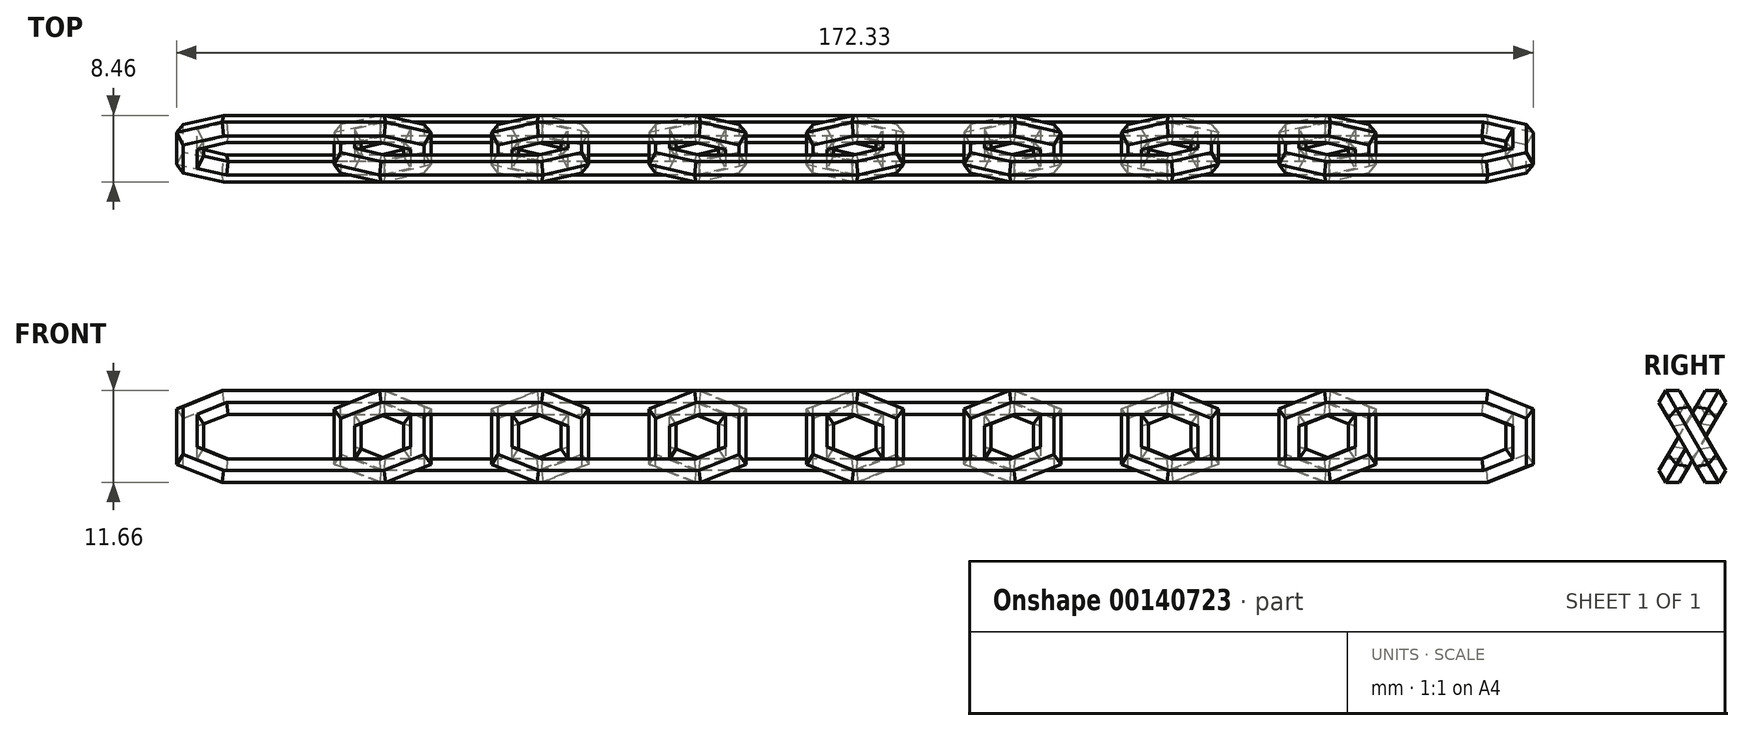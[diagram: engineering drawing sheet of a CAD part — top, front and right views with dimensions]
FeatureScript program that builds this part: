
annotation { "Feature Type Name" : "Feature", "Feature Type Description" : "" }
export const myFeature = defineFeature(function(context is Context, id is Id, definition is map)
    precondition{}
    {
        {
            var Q0;
            Q0=qCreatedBy(makeId("Front.planeOp"),FACE);
            var sketch = newSketch(context, id + "F0", { "sketchPlane" : qUnion([Q0])});
            skCircle(sketch, "E0.cCircle", {"center": v(-58.85, 0) * mm, "radius": 1.5 * mm, "construction": true});
            skLineSegment(sketch, "E0.0", {"start": v(-57.98, 1.5) * mm, "end": v(-57.12, 0) * mm});
            skLineSegment(sketch, "E0.1", {"start": v(-57.12, 0) * mm, "end": v(-57.98, -1.5) * mm});
            skLineSegment(sketch, "E0.2", {"start": v(-57.98, -1.5) * mm, "end": v(-59.72, -1.5) * mm});
            skLineSegment(sketch, "E0.3", {"start": v(-59.72, -1.5) * mm, "end": v(-60.58, 0) * mm});
            skLineSegment(sketch, "E0.4", {"start": v(-60.58, 0) * mm, "end": v(-59.72, 1.5) * mm});
            skLineSegment(sketch, "E0.5", {"start": v(-59.72, 1.5) * mm, "end": v(-57.98, 1.5) * mm});
            skPoint(sketch, "E0.0.midPoint", {"position": v(-57.55, 0.75) * mm});
            skSolve(sketch);
        }
        {
            var Q0;
            Q0=qCreatedBy(makeId("Top.planeOp"),FACE);
            var sketch = newSketch(context, id + "F1", { "sketchPlane" : qUnion([Q0])});
            skLineSegment(sketch, "E1.rect.bottom", {"start": v(-83.28, 5) * mm, "end": v(-63.28, 5) * mm});
            skLineSegment(sketch, "E1.rect.top", {"start": v(-83.28, -5) * mm, "end": v(-63.28, -5) * mm});
            skLineSegment(sketch, "E1.rect.left", {"start": v(-83.28, 5) * mm, "end": v(-83.28, -5) * mm, "construction": true});
            skLineSegment(sketch, "E1.rect.right", {"start": v(-63.28, 5) * mm, "end": v(-63.28, -5) * mm, "construction": true});
            skPoint(sketch, "E1.rect.middle", {"position": v(-73.28, 0) * mm});
            skLineSegment(sketch, "E2", {"start": v(-73.28, 0) * mm, "end": v(-58.85, 0) * mm, "construction": true});
            skPoint(sketch, "E2.endSnap0", {"position": v(-58.85, 0) * mm});
            skLineSegment(sketch, "E3", {"start": v(-63.28, -5) * mm, "end": v(-58.85, -2.95) * mm});
            skLineSegment(sketch, "E4", {"start": v(-58.85, -2.95) * mm, "end": v(-58.85, 2.95) * mm});
            skLineSegment(sketch, "E5", {"start": v(-58.85, 2.95) * mm, "end": v(-63.28, 5) * mm});
            skLineSegment(sketch, "E6", {"start": v(-73.28, -5) * mm, "end": v(-73.28, 5) * mm, "construction": true});
            skLineSegment(sketch, "E7.MirrorCS", {"start": v(-87.71, 2.95) * mm, "end": v(-83.28, 5) * mm});
            skLineSegment(sketch, "E8.MirrorCS", {"start": v(-87.71, -2.95) * mm, "end": v(-87.71, 2.95) * mm});
            skLineSegment(sketch, "E9.MirrorCS", {"start": v(-83.28, -5) * mm, "end": v(-87.71, -2.95) * mm});
            skSolve(sketch);
        }
        {
            var Q0;
            Q0=makeQuery(id+"F0.imprint","IMPRINT",FACE,{"disambiguationData":[TD([[makeQuery(id+"F0.imprint","IMPRINT",EDGE,{"derivedFrom":sQuery(id+"F0.wireOp",EDGE,"E0.0")}),-1.0]])]});
            var Q1;
            Q1=qConstructionFilter(qBodyType(qCreatedBy(id+"F1",EDGE),BodyType.WIRE),ConstructionObject.NO);
            sweep(context, id + "F2", {"profiles" : qUnion([Q0]), "path" : qUnion([Q1])});
        }
        {
            var Q0;
            Q0=makeQuery(id+"F2.opSweep","SWEPT_BODY",BODY,{"disambiguationData":[OSD([sQuery(id+"F0.wireOp",EDGE,"E0.0"),sQuery(id+"F0.wireOp",EDGE,"E0.1"),sQuery(id+"F0.wireOp",EDGE,"E0.2"),sQuery(id+"F0.wireOp",EDGE,"E0.3"),sQuery(id+"F0.wireOp",EDGE,"E0.4"),sQuery(id+"F0.wireOp",EDGE,"E0.5"),sQuery(id+"F1.wireOp",EDGE,"E9.MirrorCS")])]});
            var Q1;
            Q1=sQuery(id+"F1.wireOp",EDGE,"E2");
            transform(context, id + "F3", {"entities" : qUnion([Q0]), "transformType" : TransformType.ROTATION, "transformAxis" : qUnion([Q1]), "angle" : 60 * degree, "makeCopy" : false});
        }
        {
            var Q0;
            Q0=makeQuery(id+"F2.opSweep","SWEPT_BODY",BODY,{"disambiguationData":[OSD([sQuery(id+"F0.wireOp",EDGE,"E0.0"),sQuery(id+"F0.wireOp",EDGE,"E0.1"),sQuery(id+"F0.wireOp",EDGE,"E0.2"),sQuery(id+"F0.wireOp",EDGE,"E0.3"),sQuery(id+"F0.wireOp",EDGE,"E0.4"),sQuery(id+"F0.wireOp",EDGE,"E0.5"),sQuery(id+"F1.wireOp",EDGE,"E9.MirrorCS")])]});
            var Q1;
            Q1=qCreatedBy(makeId("Front.planeOp"),FACE);
            mirror(context, id + "F4", {"entities" : qUnion([Q0]), "mirrorPlane" : qUnion([Q1])});
        }
        {
            var Q0;
            Q0=makeQuery(id+"F4.opPattern","COPY",BODY,{"derivedFrom":makeQuery(id+"F2.opSweep","SWEPT_BODY",BODY,{"disambiguationData":[OSD([sQuery(id+"F0.wireOp",EDGE,"E0.0"),sQuery(id+"F0.wireOp",EDGE,"E0.1"),sQuery(id+"F0.wireOp",EDGE,"E0.2"),sQuery(id+"F0.wireOp",EDGE,"E0.3"),sQuery(id+"F0.wireOp",EDGE,"E0.4"),sQuery(id+"F0.wireOp",EDGE,"E0.5"),sQuery(id+"F1.wireOp",EDGE,"E9.MirrorCS")])]}),"instanceName":"1"});
            transform(context, id + "F5", {"entities" : qUnion([Q0]), "transformType" : TransformType.TRANSLATION_3D, "dx" : 20 * mm, "dy" : 0 * mm, "dz" : 0 * mm, "makeCopy" : false});
        }
        {
            var Q0;
            Q0=makeQuery(id+"F2.opSweep","SWEPT_BODY",BODY,{"disambiguationData":[OSD([sQuery(id+"F0.wireOp",EDGE,"E0.0"),sQuery(id+"F0.wireOp",EDGE,"E0.1"),sQuery(id+"F0.wireOp",EDGE,"E0.2"),sQuery(id+"F0.wireOp",EDGE,"E0.3"),sQuery(id+"F0.wireOp",EDGE,"E0.4"),sQuery(id+"F0.wireOp",EDGE,"E0.5"),sQuery(id+"F1.wireOp",EDGE,"E9.MirrorCS")])]});
            var Q1;
            Q1=makeQuery(id+"F4.opPattern","COPY",BODY,{"derivedFrom":makeQuery(id+"F2.opSweep","SWEPT_BODY",BODY,{"disambiguationData":[OSD([sQuery(id+"F0.wireOp",EDGE,"E0.0"),sQuery(id+"F0.wireOp",EDGE,"E0.1"),sQuery(id+"F0.wireOp",EDGE,"E0.2"),sQuery(id+"F0.wireOp",EDGE,"E0.3"),sQuery(id+"F0.wireOp",EDGE,"E0.4"),sQuery(id+"F0.wireOp",EDGE,"E0.5"),sQuery(id+"F1.wireOp",EDGE,"E9.MirrorCS")])]}),"instanceName":"1"});
            transform(context, id + "F6", {"entities" : qUnion([Q0, Q1]), "transformType" : TransformType.TRANSLATION_3D, "dx" : 40 * mm, "dy" : 0 * mm, "dz" : 0 * mm, "makeCopy" : true});
        }
        {
            var Q0;
            Q0=makeQuery(id+"F2.opSweep","SWEPT_BODY",BODY,{"disambiguationData":[OSD([sQuery(id+"F0.wireOp",EDGE,"E0.0"),sQuery(id+"F0.wireOp",EDGE,"E0.1"),sQuery(id+"F0.wireOp",EDGE,"E0.2"),sQuery(id+"F0.wireOp",EDGE,"E0.3"),sQuery(id+"F0.wireOp",EDGE,"E0.4"),sQuery(id+"F0.wireOp",EDGE,"E0.5"),sQuery(id+"F1.wireOp",EDGE,"E9.MirrorCS")])]});
            var Q1;
            Q1=makeQuery(id+"F4.opPattern","COPY",BODY,{"derivedFrom":makeQuery(id+"F2.opSweep","SWEPT_BODY",BODY,{"disambiguationData":[OSD([sQuery(id+"F0.wireOp",EDGE,"E0.0"),sQuery(id+"F0.wireOp",EDGE,"E0.1"),sQuery(id+"F0.wireOp",EDGE,"E0.2"),sQuery(id+"F0.wireOp",EDGE,"E0.3"),sQuery(id+"F0.wireOp",EDGE,"E0.4"),sQuery(id+"F0.wireOp",EDGE,"E0.5"),sQuery(id+"F1.wireOp",EDGE,"E9.MirrorCS")])]}),"instanceName":"1"});
            var Q2;
            Q2=makeQuery(id+"F6.opPattern","COPY",BODY,{"derivedFrom":makeQuery(id+"F2.opSweep","SWEPT_BODY",BODY,{"disambiguationData":[OSD([sQuery(id+"F0.wireOp",EDGE,"E0.0"),sQuery(id+"F0.wireOp",EDGE,"E0.1"),sQuery(id+"F0.wireOp",EDGE,"E0.2"),sQuery(id+"F0.wireOp",EDGE,"E0.3"),sQuery(id+"F0.wireOp",EDGE,"E0.4"),sQuery(id+"F0.wireOp",EDGE,"E0.5"),sQuery(id+"F1.wireOp",EDGE,"E9.MirrorCS")])]}),"instanceName":"1"});
            var Q3;
            Q3=makeQuery(id+"F6.opPattern","COPY",BODY,{"derivedFrom":makeQuery(id+"F4.opPattern","COPY",BODY,{"derivedFrom":makeQuery(id+"F2.opSweep","SWEPT_BODY",BODY,{"disambiguationData":[OSD([sQuery(id+"F0.wireOp",EDGE,"E0.0"),sQuery(id+"F0.wireOp",EDGE,"E0.1"),sQuery(id+"F0.wireOp",EDGE,"E0.2"),sQuery(id+"F0.wireOp",EDGE,"E0.3"),sQuery(id+"F0.wireOp",EDGE,"E0.4"),sQuery(id+"F0.wireOp",EDGE,"E0.5"),sQuery(id+"F1.wireOp",EDGE,"E9.MirrorCS")])]}),"instanceName":"1"}),"instanceName":"1"});
            transform(context, id + "F7", {"entities" : qUnion([Q0, Q1, Q2, Q3]), "transformType" : TransformType.TRANSLATION_3D, "dx" : 80 * mm, "dy" : 0 * mm, "dz" : 0 * mm, "makeCopy" : true});
        }
    });
